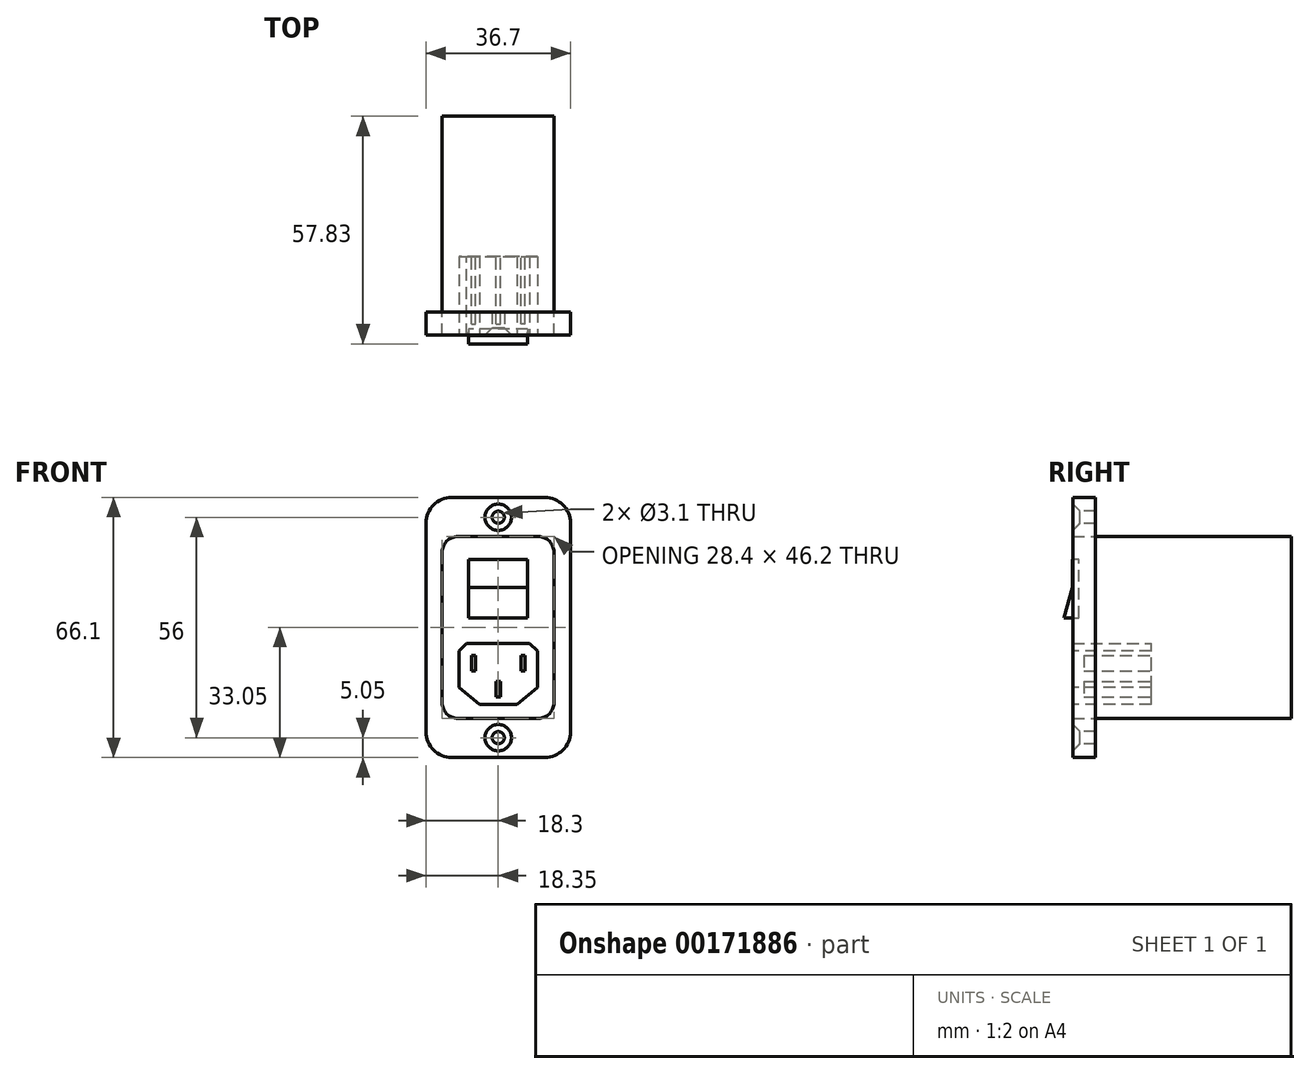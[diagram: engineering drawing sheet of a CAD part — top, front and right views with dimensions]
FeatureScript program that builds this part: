
annotation { "Feature Type Name" : "Feature", "Feature Type Description" : "" }
export const myFeature = defineFeature(function(context is Context, id is Id, definition is map)
    precondition{}
    {
        {
            var Q0;
            Q0=qCreatedBy(makeId("Front.planeOp"),FACE);
            var sketch = newSketch(context, id + "F0", { "sketchPlane" : qUnion([Q0])});
            skLineSegment(sketch, "E0.bottom", {"start": v(-10.25, 23.1) * mm, "end": v(10.15, 23.1) * mm});
            skLineSegment(sketch, "E0.top", {"start": v(-10.25, -23.1) * mm, "end": v(10.15, -23.1) * mm});
            skLineSegment(sketch, "E0.left", {"start": v(-14.25, 19.1) * mm, "end": v(-14.25, -19.1) * mm});
            skLineSegment(sketch, "E0.right", {"start": v(14.15, 19.1) * mm, "end": v(14.15, -19.1) * mm});
            skLineSegment(sketch, "E1", {"start": v(-100.57, 0) * mm, "end": v(-8.57, 0) * mm, "construction": true});
            skPoint(sketch, "E2.visualSharp", {"position": v(14.15, 23.1) * mm});
            skArc(sketch, "E2.filletArc", {"start": v(14.15, 19.1) * mm, "mid": v(12.98, 21.93) * mm, "end": v(10.15, 23.1) * mm});
            skPoint(sketch, "E3.visualSharp", {"position": v(-14.25, 23.1) * mm});
            skArc(sketch, "E3.filletArc", {"start": v(-10.25, 23.1) * mm, "mid": v(-13.08, 21.93) * mm, "end": v(-14.25, 19.1) * mm});
            skPoint(sketch, "E4.visualSharp", {"position": v(-14.25, -23.1) * mm});
            skArc(sketch, "E4.filletArc", {"start": v(-14.25, -19.1) * mm, "mid": v(-13.08, -21.93) * mm, "end": v(-10.25, -23.1) * mm});
            skPoint(sketch, "E5.visualSharp", {"position": v(14.15, -23.1) * mm});
            skArc(sketch, "E5.filletArc", {"start": v(10.15, -23.1) * mm, "mid": v(12.98, -21.93) * mm, "end": v(14.15, -19.1) * mm});
            skLineSegment(sketch, "E6.bottom", {"start": v(11.85, -33.05) * mm, "end": v(-11.85, -33.05) * mm});
            skLineSegment(sketch, "E6.top", {"start": v(11.85, 33.05) * mm, "end": v(-11.85, 33.05) * mm});
            skLineSegment(sketch, "E6.left", {"start": v(18.35, -26.55) * mm, "end": v(18.35, 26.55) * mm});
            skLineSegment(sketch, "E6.right", {"start": v(-18.35, -26.55) * mm, "end": v(-18.35, 26.55) * mm});
            skPoint(sketch, "E6.middle", {"position": v(0, 0) * mm});
            skPoint(sketch, "E7.visualSharp", {"position": v(-18.35, 33.05) * mm});
            skArc(sketch, "E7.filletArc", {"start": v(-11.85, 33.05) * mm, "mid": v(-16.45, 31.15) * mm, "end": v(-18.35, 26.55) * mm});
            skPoint(sketch, "E8.visualSharp", {"position": v(18.35, 33.05) * mm});
            skArc(sketch, "E8.filletArc", {"start": v(18.35, 26.55) * mm, "mid": v(16.45, 31.15) * mm, "end": v(11.85, 33.05) * mm});
            skPoint(sketch, "E9.visualSharp", {"position": v(18.35, -33.05) * mm});
            skArc(sketch, "E9.filletArc", {"start": v(11.85, -33.05) * mm, "mid": v(16.45, -31.15) * mm, "end": v(18.35, -26.55) * mm});
            skPoint(sketch, "E10.visualSharp", {"position": v(-18.35, -33.05) * mm});
            skArc(sketch, "E10.filletArc", {"start": v(-18.35, -26.55) * mm, "mid": v(-16.45, -31.15) * mm, "end": v(-11.85, -33.05) * mm});
            skSolve(sketch);
        }
        {
            var Q0;
            Q0 = qSketchRegion(id + "F0", true);
            extrude(context, id + "F1", {"entities" : qUnion([Q0]), "depth" : 5.8 * mm});
        }
        {
            var Q0;
            Q0=makeQuery(id+"F0.imprint","IMPRINT",FACE,{"disambiguationData":[TD([[makeQuery(id+"F0.imprint","IMPRINT",EDGE,{"derivedFrom":sQuery(id+"F0.wireOp",EDGE,"E0.bottom")}),-1.0]])]});
            extrude(context, id + "F2", {"entities" : qUnion([Q0]), "depth" : 5.8 * mm, "hasSecondDirection" : true, "secondDirectionOppositeDirection" : true, "secondDirectionDepth" : 49.8 * mm});
        }
        {
            var Q0;
            Q0=makeQuery(id+"F1.opExtrude","CAP_FACE",FACE,{"disambiguationData":[OSD([sQuery(id+"F0.wireOp",EDGE,"E0.bottom"),sQuery(id+"F0.wireOp",EDGE,"E0.top"),sQuery(id+"F0.wireOp",EDGE,"E0.left"),sQuery(id+"F0.wireOp",EDGE,"E0.right"),sQuery(id+"F0.wireOp",EDGE,"E2.filletArc"),sQuery(id+"F0.wireOp",EDGE,"E3.filletArc"),sQuery(id+"F0.wireOp",EDGE,"E4.filletArc"),sQuery(id+"F0.wireOp",EDGE,"E5.filletArc"),sQuery(id+"F0.wireOp",EDGE,"E6.bottom"),sQuery(id+"F0.wireOp",EDGE,"E6.top"),sQuery(id+"F0.wireOp",EDGE,"E6.left"),sQuery(id+"F0.wireOp",EDGE,"E6.right"),sQuery(id+"F0.wireOp",EDGE,"E7.filletArc"),sQuery(id+"F0.wireOp",EDGE,"E8.filletArc"),sQuery(id+"F0.wireOp",EDGE,"E9.filletArc"),sQuery(id+"F0.wireOp",EDGE,"E10.filletArc")])],"isStart":false});
            var sketch = newSketch(context, id + "F3", { "sketchPlane" : qUnion([Q0])});
            skLineSegment(sketch, "E11", {"start": v(-9.4, 28) * mm, "end": v(9.42, 28) * mm, "construction": true});
            skLineSegment(sketch, "E12.MirrorCS", {"start": v(-9.4, -28) * mm, "end": v(9.42, -28) * mm, "construction": true});
            skLineSegment(sketch, "E13", {"start": v(0, 31.17) * mm, "end": v(0, -30.42) * mm, "construction": true});
            skPoint(sketch, "E14", {"position": v(0, -28) * mm});
            skPoint(sketch, "E15", {"position": v(0, 28) * mm});
            skSolve(sketch);
        }
        {
            var Q0;
            Q0=sQuery(id+"F3.wireOp",VERTEX,"E15");
            var Q1;
            Q1=sQuery(id+"F3.wireOp",VERTEX,"E14");
            var Q2;
            Q2=makeQuery(id+"F1.opExtrude","SWEPT_BODY",BODY,{"disambiguationData":[OSD([sQuery(id+"F0.wireOp",EDGE,"E0.bottom"),sQuery(id+"F0.wireOp",EDGE,"E0.top"),sQuery(id+"F0.wireOp",EDGE,"E0.left"),sQuery(id+"F0.wireOp",EDGE,"E0.right"),sQuery(id+"F0.wireOp",EDGE,"E2.filletArc"),sQuery(id+"F0.wireOp",EDGE,"E3.filletArc"),sQuery(id+"F0.wireOp",EDGE,"E4.filletArc"),sQuery(id+"F0.wireOp",EDGE,"E5.filletArc"),sQuery(id+"F0.wireOp",EDGE,"E6.bottom"),sQuery(id+"F0.wireOp",EDGE,"E6.top"),sQuery(id+"F0.wireOp",EDGE,"E6.left"),sQuery(id+"F0.wireOp",EDGE,"E6.right"),sQuery(id+"F0.wireOp",EDGE,"E7.filletArc"),sQuery(id+"F0.wireOp",EDGE,"E8.filletArc"),sQuery(id+"F0.wireOp",EDGE,"E9.filletArc"),sQuery(id+"F0.wireOp",EDGE,"E10.filletArc")])]});
            hole(context, id + "F4", {"style" : HoleStyle.C_SINK, "endStyle" : HoleEndStyle.THROUGH, "holeDiameter" : 3.1 * mm, "cSinkDiameter" : 6.72 * mm, "cSinkAngle" : 90 * degree, "startFromSketch" : true, "locations" : qUnion([Q0, Q1]), "scope" : qUnion([Q2]), "isTappedThrough" : true});
        }
        {
            var Q0;
            Q0=makeQuery(id+"F2.opExtrude","CAP_FACE",FACE,{"disambiguationData":[OSD([sQuery(id+"F0.wireOp",EDGE,"E0.bottom"),sQuery(id+"F0.wireOp",EDGE,"E0.top"),sQuery(id+"F0.wireOp",EDGE,"E0.left"),sQuery(id+"F0.wireOp",EDGE,"E0.right"),sQuery(id+"F0.wireOp",EDGE,"E2.filletArc"),sQuery(id+"F0.wireOp",EDGE,"E3.filletArc"),sQuery(id+"F0.wireOp",EDGE,"E4.filletArc"),sQuery(id+"F0.wireOp",EDGE,"E5.filletArc")])],"isStart":false});
            var sketch = newSketch(context, id + "F5", { "sketchPlane" : qUnion([Q0])});
            skLineSegment(sketch, "E16", {"start": v(-10, -4) * mm, "end": v(10, -4) * mm});
            skLineSegment(sketch, "E17", {"start": v(10, -4) * mm, "end": v(10, -15.28) * mm});
            skLineSegment(sketch, "E18", {"start": v(10, -15.28) * mm, "end": v(4.75, -19.5) * mm});
            skLineSegment(sketch, "E19", {"start": v(4.75, -19.5) * mm, "end": v(-4.75, -19.5) * mm});
            skLineSegment(sketch, "E20", {"start": v(-4.75, -19.5) * mm, "end": v(-10, -15.28) * mm});
            skLineSegment(sketch, "E21", {"start": v(-10, -15.28) * mm, "end": v(-10, -4) * mm});
            skSolve(sketch);
        }
        {
            var Q0;
            Q0=makeQuery(id+"F5.imprint","IMPRINT",FACE,{"disambiguationData":[TD([[makeQuery(id+"F5.imprint","IMPRINT",EDGE,{"derivedFrom":sQuery(id+"F5.wireOp",EDGE,"E16")}),-1.0]])]});
            extrude(context, id + "F6", {"entities" : qUnion([Q0]), "operationType" : NewBodyOperationType.REMOVE, "oppositeDirection" : true, "depth" : 20 * mm});
        }
        {
            var Q0;
            Q0=makeQuery(id+"F6.boolean.opBoolean","COPY",EDGE,{"derivedFrom":makeQuery(id+"F6.opExtrude","SWEPT_EDGE",EDGE,{"disambiguationData":[OSD([sQuery(id+"F5.wireOp",EDGE,"E16"),sQuery(id+"F5.wireOp",EDGE,"E17")])]})});
            var Q1;
            Q1=makeQuery(id+"F6.boolean.opBoolean","COPY",EDGE,{"derivedFrom":makeQuery(id+"F6.opExtrude","SWEPT_EDGE",EDGE,{"disambiguationData":[OSD([sQuery(id+"F5.wireOp",EDGE,"E16"),sQuery(id+"F5.wireOp",EDGE,"E21")])]})});
            chamfer(context, id + "F7", {"entities" : qUnion([Q0, Q1]), "width" : 2 * mm, "tangentPropagation" : true});
        }
        {
            var Q0;
            Q0=makeQuery(id+"F0.imprint","IMPRINT",FACE,{"disambiguationData":[TD([[makeQuery(id+"F0.imprint","IMPRINT",EDGE,{"derivedFrom":sQuery(id+"F0.wireOp",EDGE,"E0.bottom")}),-1.0]])]});
            var sketch = newSketch(context, id + "F8", { "sketchPlane" : qUnion([Q0])});
            skLineSegment(sketch, "E22.bottom", {"start": v(-6.84, -7.13) * mm, "end": v(-5.74, -7.13) * mm});
            skLineSegment(sketch, "E22.top", {"start": v(-6.84, -11.08) * mm, "end": v(-5.74, -11.08) * mm});
            skLineSegment(sketch, "E22.left", {"start": v(-6.84, -7.13) * mm, "end": v(-6.84, -11.08) * mm});
            skLineSegment(sketch, "E22.right", {"start": v(-5.74, -7.13) * mm, "end": v(-5.74, -11.08) * mm});
            skLineSegment(sketch, "E23.MirrorCS", {"start": v(6.84, -7.13) * mm, "end": v(6.84, -11.08) * mm});
            skLineSegment(sketch, "E24.MirrorCS", {"start": v(5.74, -7.13) * mm, "end": v(5.74, -11.08) * mm});
            skLineSegment(sketch, "E25.MirrorCS", {"start": v(6.84, -7.13) * mm, "end": v(5.74, -7.13) * mm});
            skLineSegment(sketch, "E26.MirrorCS", {"start": v(6.84, -11.08) * mm, "end": v(5.74, -11.08) * mm});
            skLineSegment(sketch, "E27.1.0.0", {"start": v(-0.58, -13.73) * mm, "end": v(0.53, -13.73) * mm});
            skLineSegment(sketch, "E27.1.0.1", {"start": v(0.53, -13.73) * mm, "end": v(0.53, -17.68) * mm});
            skLineSegment(sketch, "E27.1.0.2", {"start": v(-0.58, -13.73) * mm, "end": v(-0.58, -17.68) * mm});
            skLineSegment(sketch, "E27.1.0.3", {"start": v(-0.58, -17.68) * mm, "end": v(0.53, -17.68) * mm});
            skLineSegment(sketch, "E27.direction1", {"start": v(-6.84, -7.13) * mm, "end": v(-0.58, -13.73) * mm, "construction": true});
            skSolve(sketch);
        }
        {
            var Q0;
            Q0 = qSketchRegion(id + "F8", true);
            extrude(context, id + "F9", {"entities" : qUnion([Q0]), "operationType" : NewBodyOperationType.ADD, "depth" : 3 * mm, "hasSecondDirection" : true, "secondDirectionOppositeDirection" : true, "secondDirectionDepth" : 15 * mm});
        }
        {
            var Q0;
            Q0=qCreatedBy(makeId("Right.planeOp"),FACE);
            var sketch = newSketch(context, id + "F10", { "sketchPlane" : qUnion([Q0])});
            skLineSegment(sketch, "E28", {"start": v(-5.8, 22.98) * mm, "end": v(-5.8, -9.29) * mm, "construction": true});
            skLineSegment(sketch, "E29", {"start": v(-5.8, 17.32) * mm, "end": v(-5.8, 10.18) * mm});
            skLineSegment(sketch, "E30", {"start": v(-5.91, 10.18) * mm, "end": v(-8.03, 2.47) * mm});
            skLineSegment(sketch, "E31", {"start": v(-8.03, 2.47) * mm, "end": v(-4.29, 2.47) * mm});
            skLineSegment(sketch, "E32", {"start": v(-4.29, 2.47) * mm, "end": v(-4.29, 17.32) * mm});
            skLineSegment(sketch, "E33", {"start": v(-4.29, 17.32) * mm, "end": v(-5.91, 17.32) * mm});
            skLineSegment(sketch, "E34", {"start": v(-5.91, 17.32) * mm, "end": v(-5.91, 10.18) * mm});
            skSolve(sketch);
        }
        {
            var Q0;
            Q0 = qSketchRegion(id + "F10", true);
            extrude(context, id + "F11", {"entities" : qUnion([Q0]), "endBound" : BoundingType.SYMMETRIC, "depth" : 15 * mm});
        }
    });
